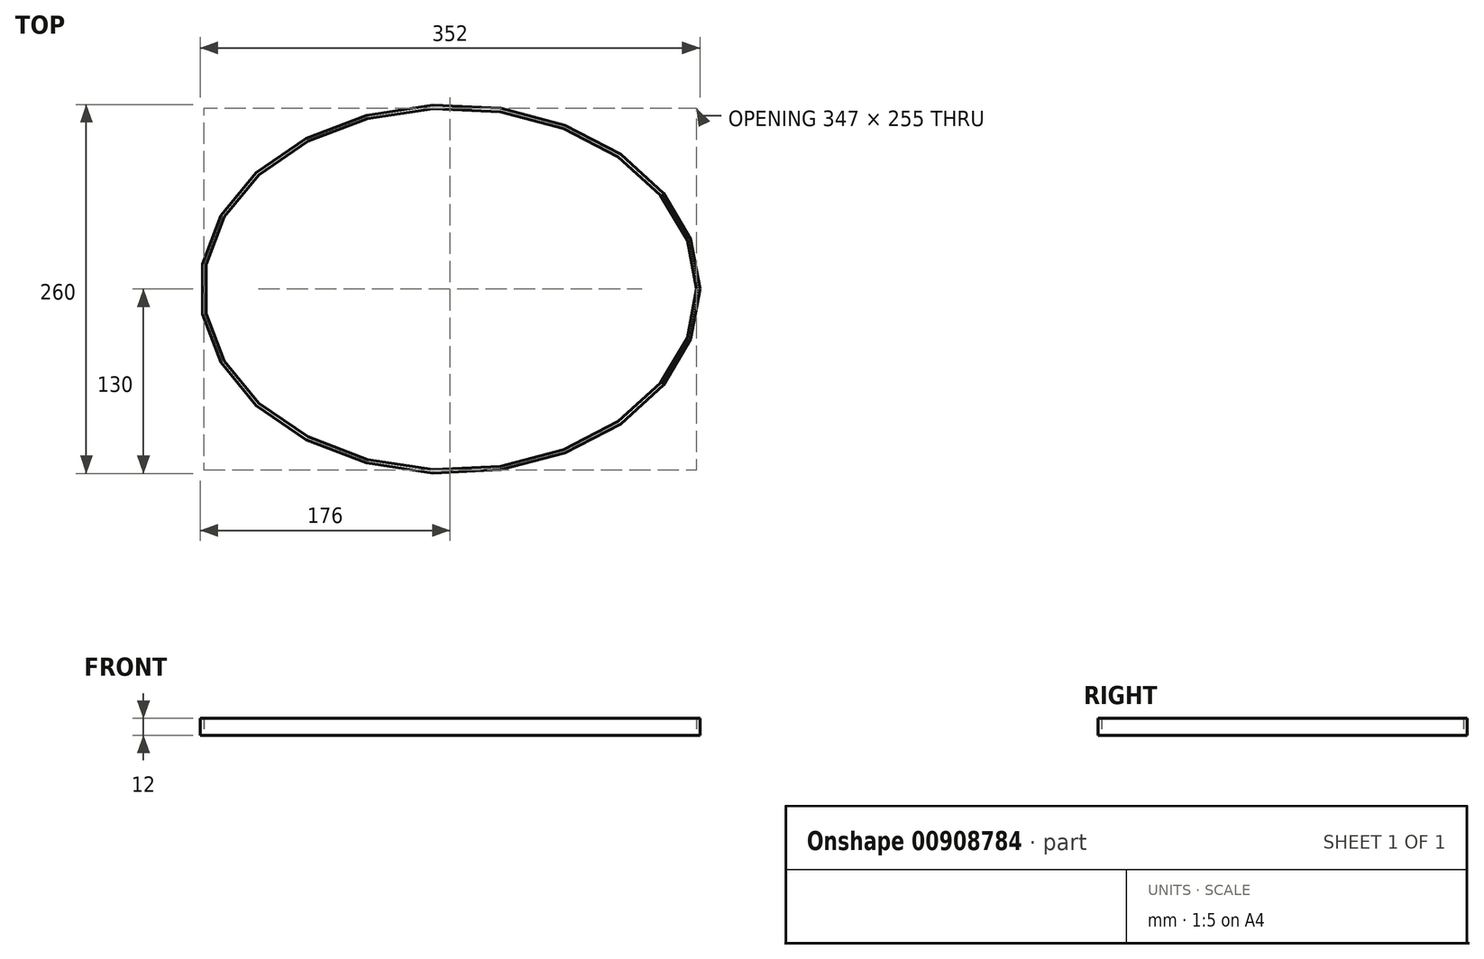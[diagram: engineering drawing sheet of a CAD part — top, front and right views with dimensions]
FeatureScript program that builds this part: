
annotation { "Feature Type Name" : "Feature", "Feature Type Description" : "" }
export const myFeature = defineFeature(function(context is Context, id is Id, definition is map)
    precondition{}
    {
        {
            var Q0;
            Q0=qCreatedBy(makeId("Top.planeOp"),FACE);
            var sketch = newSketch(context, id + "F0", { "sketchPlane" : qUnion([Q0])});
            skEllipse(sketch, "E0", {"center": v(0, 0) * mm, "majorRadius": 173.5 * mm, "minorRadius": 127.5 * mm, "majorAxis": v(1, 0)});
            skEllipse(sketch, "E1", {"center": v(0, 0) * mm, "majorRadius": 176 * mm, "minorRadius": 130 * mm, "majorAxis": v(1, 0)});
            skSolve(sketch);
        }
        {
            var Q0;
            Q0 = qSketchRegion(id + "F0", true);
            extrude(context, id + "F1", {"entities" : qUnion([Q0]), "depth" : 12 * mm, "offsetDistance" : 25 * mm});
        }
    });
